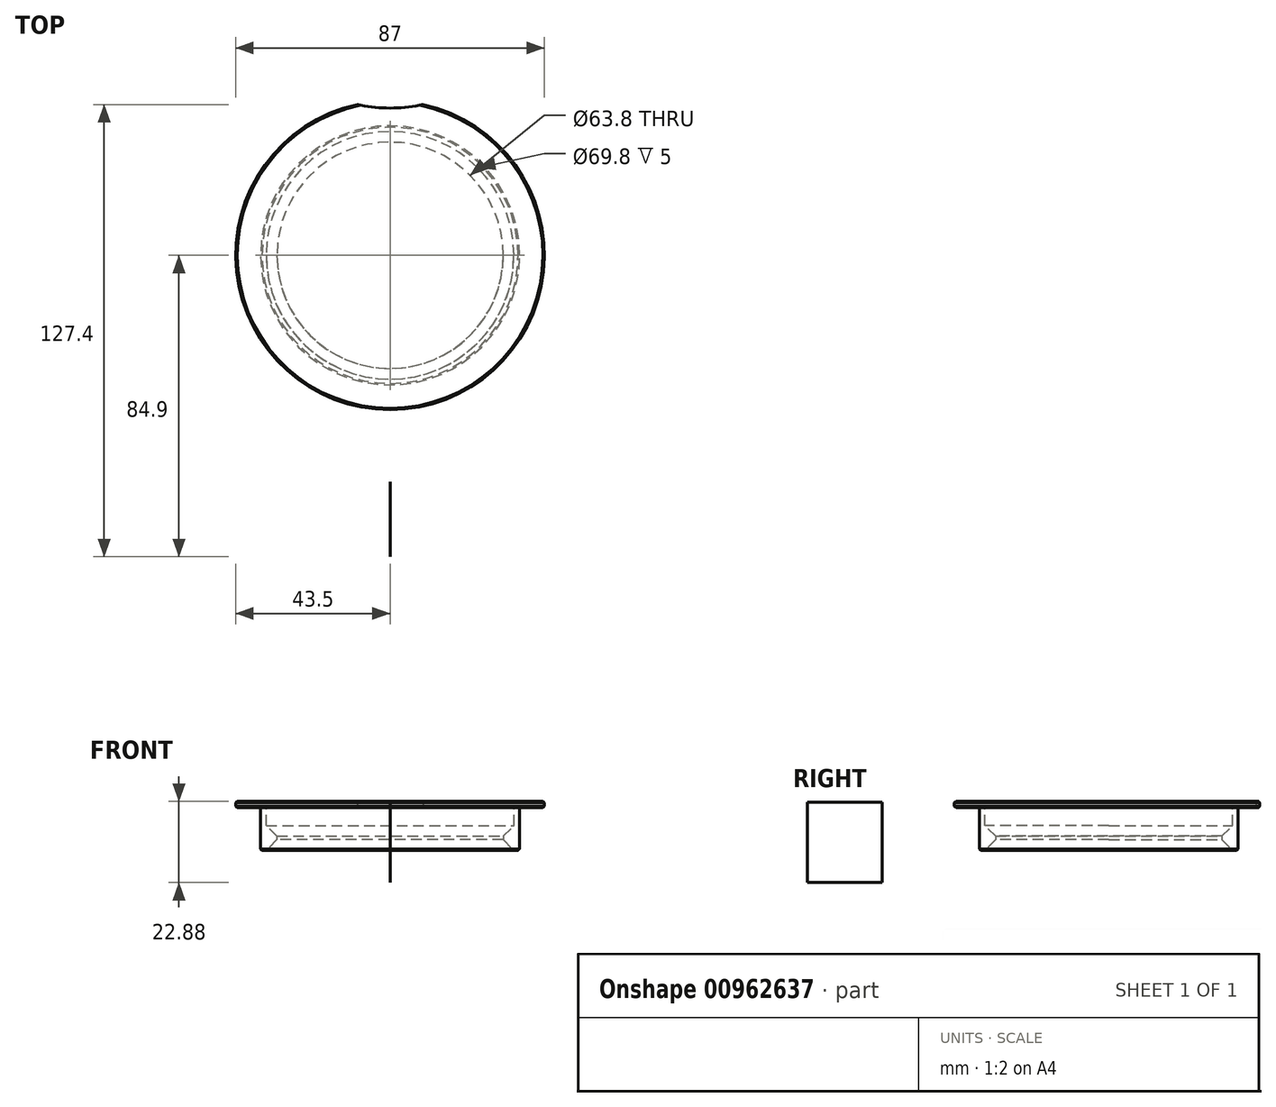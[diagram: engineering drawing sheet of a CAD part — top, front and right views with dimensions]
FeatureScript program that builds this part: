
annotation { "Feature Type Name" : "Feature", "Feature Type Description" : "" }
export const myFeature = defineFeature(function(context is Context, id is Id, definition is map)
    precondition{}
    {
        {
            var Q0;
            Q0=qCreatedBy(makeId("Top.planeOp"),FACE);
            var sketch = newSketch(context, id + "F0", { "sketchPlane" : qUnion([Q0])});
            skCircle(sketch, "E0", {"center": v(0, 0) * mm, "radius": 36.5 * mm});
            skCircle(sketch, "E1", {"center": v(0, 0) * mm, "radius": 43.5 * mm});
            skCircle(sketch, "E2", {"center": v(0, 0) * mm, "radius": 34.9 * mm});
            skCircle(sketch, "E3", {"center": v(0, 0) * mm, "radius": 18.9 * mm, "construction": true});
            skCircle(sketch, "E4", {"center": v(0, 0) * mm, "radius": 16.9 * mm, "construction": true});
            skCircle(sketch, "E5", {"center": v(0, 0) * mm, "radius": 22.9 * mm, "construction": true});
            skLineSegment(sketch, "E6", {"start": v(0, 0) * mm, "end": v(0, 142.24) * mm, "construction": true});
            skCircle(sketch, "E7", {"center": v(0, 85) * mm, "radius": 43.5 * mm, "construction": true});
            skArc(sketch, "E8", {"start": v(-9.27, 42.5) * mm, "mid": v(0, 41.5) * mm, "end": v(9.27, 42.5) * mm});
            skSolve(sketch);
        }
        {
            var Q0;
            Q0=makeQuery(id+"F0.imprint","IMPRINT",FACE,{"disambiguationData":[TD([[makeQuery(id+"F0.imprint","IMPRINT",EDGE,{"derivedFrom":sQuery(id+"F0.wireOp",EDGE,"E0")}),-1.0]])]});
            var Q1;
            Q1=makeQuery(id+"F0.imprint","IMPRINT",FACE,{"disambiguationData":[TD([[makeQuery(id+"F0.imprint","IMPRINT",EDGE,{"derivedFrom":sQuery(id+"F0.wireOp",EDGE,"E0")}),1.0]])]});
            var Q2;
            Q2=makeQuery(id+"F0.imprint","IMPRINT",FACE,{"disambiguationData":[TD([[makeQuery(id+"F0.imprint","IMPRINT",EDGE,{"derivedFrom":sQuery(id+"F0.wireOp",EDGE,"E3")}),1.0]])]});
            var Q3;
            Q3=makeQuery(id+"F0.imprint","IMPRINT",FACE,{"disambiguationData":[TD([[makeQuery(id+"F0.imprint","IMPRINT",EDGE,{"derivedFrom":sQuery(id+"F0.wireOp",EDGE,"E3")}),-1.0]])]});
            var Q4;
            Q4=makeQuery(id+"F0.imprint","IMPRINT",FACE,{"disambiguationData":[TD([[makeQuery(id+"F0.imprint","IMPRINT",EDGE,{"derivedFrom":sQuery(id+"F0.wireOp",EDGE,"E2")}),1.0]])]});
            var Q5;
            Q5=makeQuery(id+"F0.imprint","IMPRINT",FACE,{"disambiguationData":[TD([[makeQuery(id+"F0.imprint","IMPRINT",EDGE,{"derivedFrom":sQuery(id+"F0.wireOp",EDGE,"E4")}),1.0]])]});
            extrude(context, id + "F1", {"entities" : qUnion([Q0, Q1, Q2, Q3, Q4, Q5]), "depth" : 1.8 * mm, "offsetDistance" : 25 * mm});
        }
        {
            var Q0;
            Q0=makeQuery(id+"F0.imprint","IMPRINT",FACE,{"disambiguationData":[TD([[makeQuery(id+"F0.imprint","IMPRINT",EDGE,{"derivedFrom":sQuery(id+"F0.wireOp",EDGE,"E0")}),1.0]])]});
            extrude(context, id + "F2", {"entities" : qUnion([Q0]), "operationType" : NewBodyOperationType.ADD, "oppositeDirection" : true, "depth" : 12 * mm, "offsetDistance" : 25 * mm});
        }
        {
            var Q0;
            Q0=makeQuery(id+"F2.opExtrude","CAP_FACE",FACE,{"disambiguationData":[OSD([sQuery(id+"F0.wireOp",EDGE,"E0"),sQuery(id+"F0.wireOp",EDGE,"E2")])],"isStart":false});
            var sketch = newSketch(context, id + "F3", { "sketchPlane" : qUnion([Q0])});
            skCircle(sketch, "E9.0", {"center": v(0, 0) * mm, "radius": 34.9 * mm});
            skCircle(sketch, "E10", {"center": v(0, 0) * mm, "radius": 31.9 * mm});
            skSolve(sketch);
        }
        {
            var Q0;
            Q0 = qSketchRegion(id + "F3", true);
            extrude(context, id + "F4", {"entities" : qUnion([Q0]), "operationType" : NewBodyOperationType.ADD, "oppositeDirection" : true, "depth" : 7 * mm, "offsetDistance" : 25 * mm});
        }
        {
            var Q0;
            Q0=makeQuery(id+"F4.opExtrude","CAP_EDGE",EDGE,{"disambiguationData":[OSD([sQuery(id+"F3.wireOp",EDGE,"E10")])],"isStart":true});
            var Q1;
            Q1=makeQuery(id+"F4.opExtrude","CAP_EDGE",EDGE,{"disambiguationData":[OSD([sQuery(id+"F3.wireOp",EDGE,"E10")])],"isStart":false});
            chamfer(context, id + "F5", {"entities" : qUnion([Q0, Q1]), "width" : 3 * mm, "tangentPropagation" : true});
        }
        {
            var Q0;
            Q0=qCreatedBy(makeId("Right.planeOp"),FACE);
            var sketch = newSketch(context, id + "F6", { "sketchPlane" : qUnion([Q0])});
            skLineSegment(sketch, "E11.bottom", {"start": v(-84.9, 1.53) * mm, "end": v(-63.87, 1.53) * mm});
            skLineSegment(sketch, "E11.top", {"start": v(-84.9, -21.08) * mm, "end": v(-63.87, -21.08) * mm});
            skLineSegment(sketch, "E11.left", {"start": v(-84.9, 1.53) * mm, "end": v(-84.9, -21.08) * mm});
            skLineSegment(sketch, "E11.right", {"start": v(-63.87, 1.53) * mm, "end": v(-63.87, -21.08) * mm});
            skPoint(sketch, "E11.middle", {"position": v(-74.39, -9.78) * mm});
            skSolve(sketch);
        }
        {
            var Q0;
            Q0 = qSketchRegion(id + "F6", true);
            extrude(context, id + "F7", {"entities" : qUnion([Q0]), "depth" : 0.1 * mm, "offsetDistance" : 25 * mm});
        }
        {
            var Q0;
            Q0=makeQuery(id+"F1.opExtrude","CAP_EDGE",EDGE,{"disambiguationData":[OSD([sQuery(id+"F0.wireOp",EDGE,"E1")])],"isStart":false});
            var Q1;
            Q1=makeQuery(id+"F1.opExtrude","CAP_EDGE",EDGE,{"disambiguationData":[OSD([sQuery(id+"F0.wireOp",EDGE,"E2")])],"isStart":false});
            var Q2;
            Q2=makeQuery(id+"F1.opExtrude","CAP_EDGE",EDGE,{"disambiguationData":[OSD([sQuery(id+"F0.wireOp",EDGE,"E5")])],"isStart":false});
            var Q3;
            Q3=makeQuery(id+"F1.opExtrude","CAP_EDGE",EDGE,{"disambiguationData":[OSD([sQuery(id+"F0.wireOp",EDGE,"E5")])],"isStart":true});
            var Q4;
            Q4=makeQuery(id+"F2.opExtrude","CAP_EDGE",EDGE,{"disambiguationData":[OSD([sQuery(id+"F0.wireOp",EDGE,"E0")])],"isStart":false});
            var Q5;
            Q5=makeQuery(id+"F1.opExtrude","CAP_EDGE",EDGE,{"disambiguationData":[OSD([sQuery(id+"F0.wireOp",EDGE,"E1")])],"isStart":true});
            var Q6;
            Q6=makeQuery(id+"F1.opExtrude","CAP_EDGE",EDGE,{"disambiguationData":[OSD([sQuery(id+"F0.wireOp",EDGE,"E4")])],"isStart":false});
            chamfer(context, id + "F8", {"entities" : qUnion([Q0, Q1, Q2, Q3, Q4, Q5, Q6]), "width" : 0.4 * mm, "tangentPropagation" : true});
        }
    });
